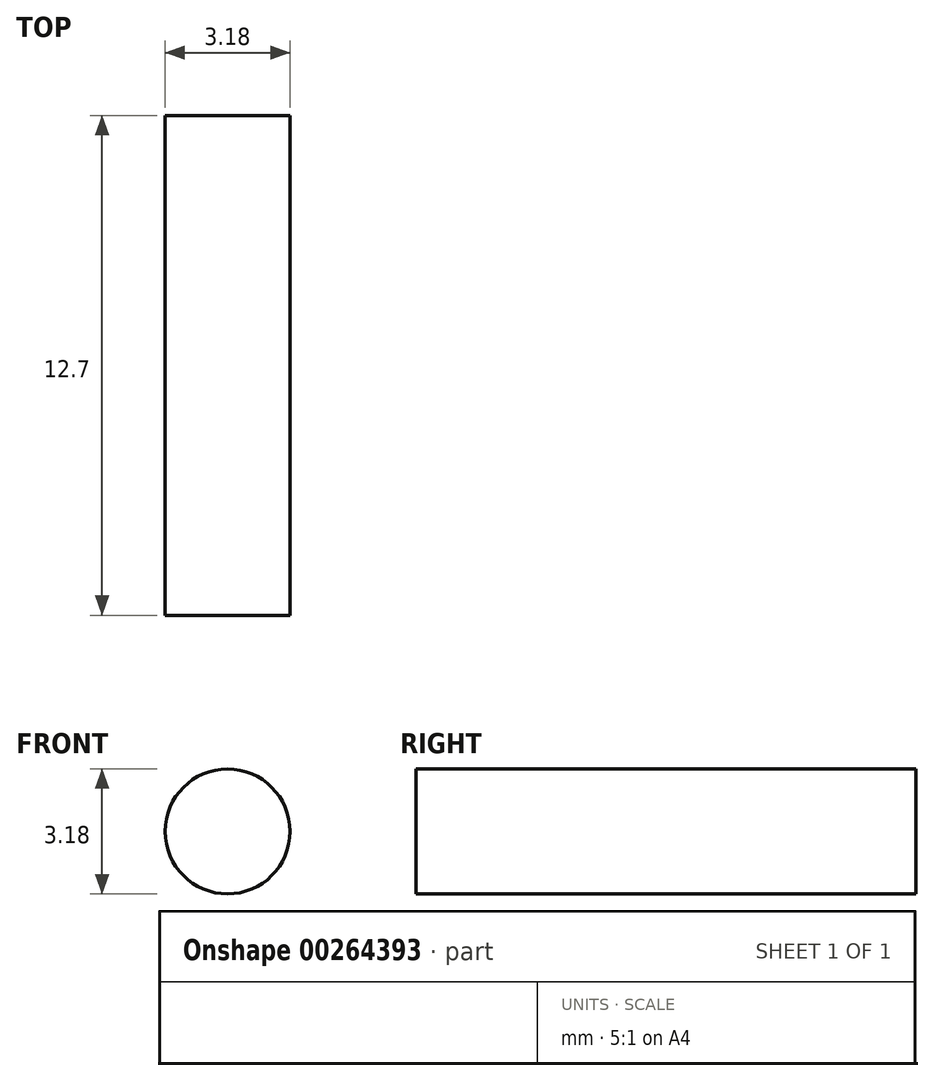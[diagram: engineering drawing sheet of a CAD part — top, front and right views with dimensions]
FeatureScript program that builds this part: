
annotation { "Feature Type Name" : "Feature", "Feature Type Description" : "" }
export const myFeature = defineFeature(function(context is Context, id is Id, definition is map)
    precondition{}
    {
        {
            var Q0;
            Q0=qCreatedBy(makeId("Front.planeOp"),FACE);
            var sketch = newSketch(context, id + "F0", { "sketchPlane" : qUnion([Q0])});
            skCircle(sketch, "E0", {"center": v(0, 0) * mm, "radius": 1.59 * mm});
            skSolve(sketch);
        }
        {
            var Q0;
            Q0=qSketchRegion(id+"F0",true);
            extrude(context, id + "F1", {"entities" : qUnion([Q0]), "depth" : 12.7 * mm});
        }
    });
